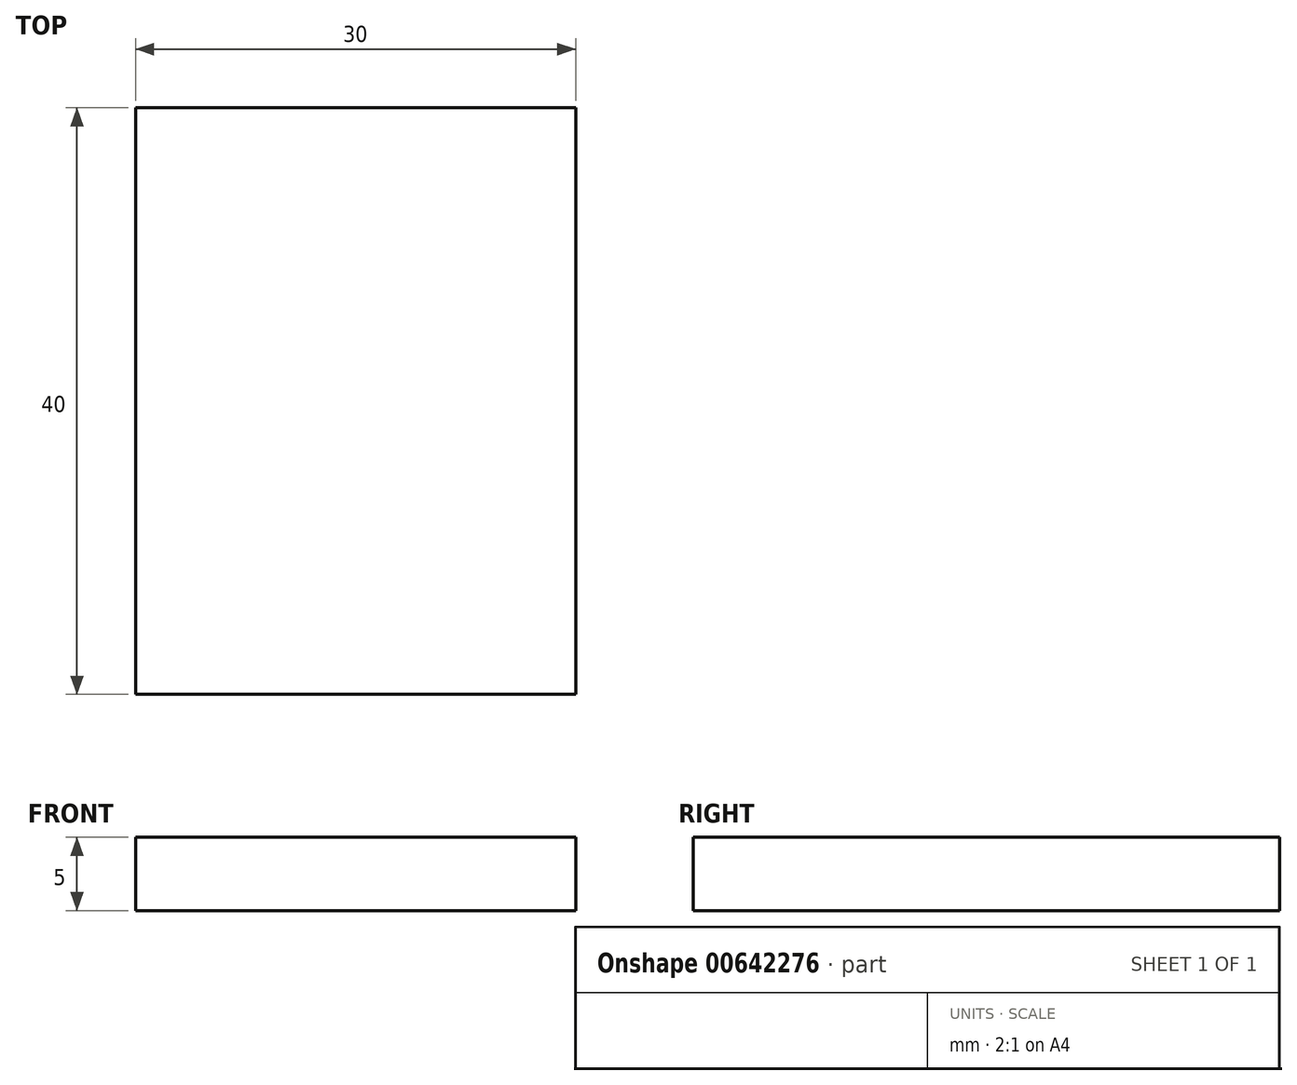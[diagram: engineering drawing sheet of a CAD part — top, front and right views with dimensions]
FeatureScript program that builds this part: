
annotation { "Feature Type Name" : "Feature", "Feature Type Description" : "" }
export const myFeature = defineFeature(function(context is Context, id is Id, definition is map)
    precondition{}
    {
        {
            var Q0;
            Q0=qCreatedBy(makeId("Front.planeOp"),FACE);
            var sketch = newSketch(context, id + "F0", { "sketchPlane" : qUnion([Q0])});
            skLineSegment(sketch, "E0.bottom", {"start": v(16.2, -2.5) * mm, "end": v(-13.8, -2.5) * mm});
            skLineSegment(sketch, "E0.top", {"start": v(16.2, 2.5) * mm, "end": v(-13.8, 2.5) * mm});
            skLineSegment(sketch, "E0.left", {"start": v(16.2, -2.5) * mm, "end": v(16.2, 2.5) * mm});
            skLineSegment(sketch, "E0.right", {"start": v(-13.8, -2.5) * mm, "end": v(-13.8, 2.5) * mm});
            skPoint(sketch, "E0.middle", {"position": v(1.2, 0) * mm});
            skSolve(sketch);
        }
        {
            var Q0;
            Q0=makeQuery(id+"F0.imprint","IMPRINT",FACE,{"disambiguationData":[TD([[makeQuery(id+"F0.imprint","IMPRINT",EDGE,{"derivedFrom":sQuery(id+"F0.wireOp",EDGE,"E0.bottom")}),-1.0]])]});
            extrude(context, id + "F1", {"entities" : qUnion([Q0]), "depth" : 40 * mm, "offsetDistance" : 25 * mm});
        }
    });
